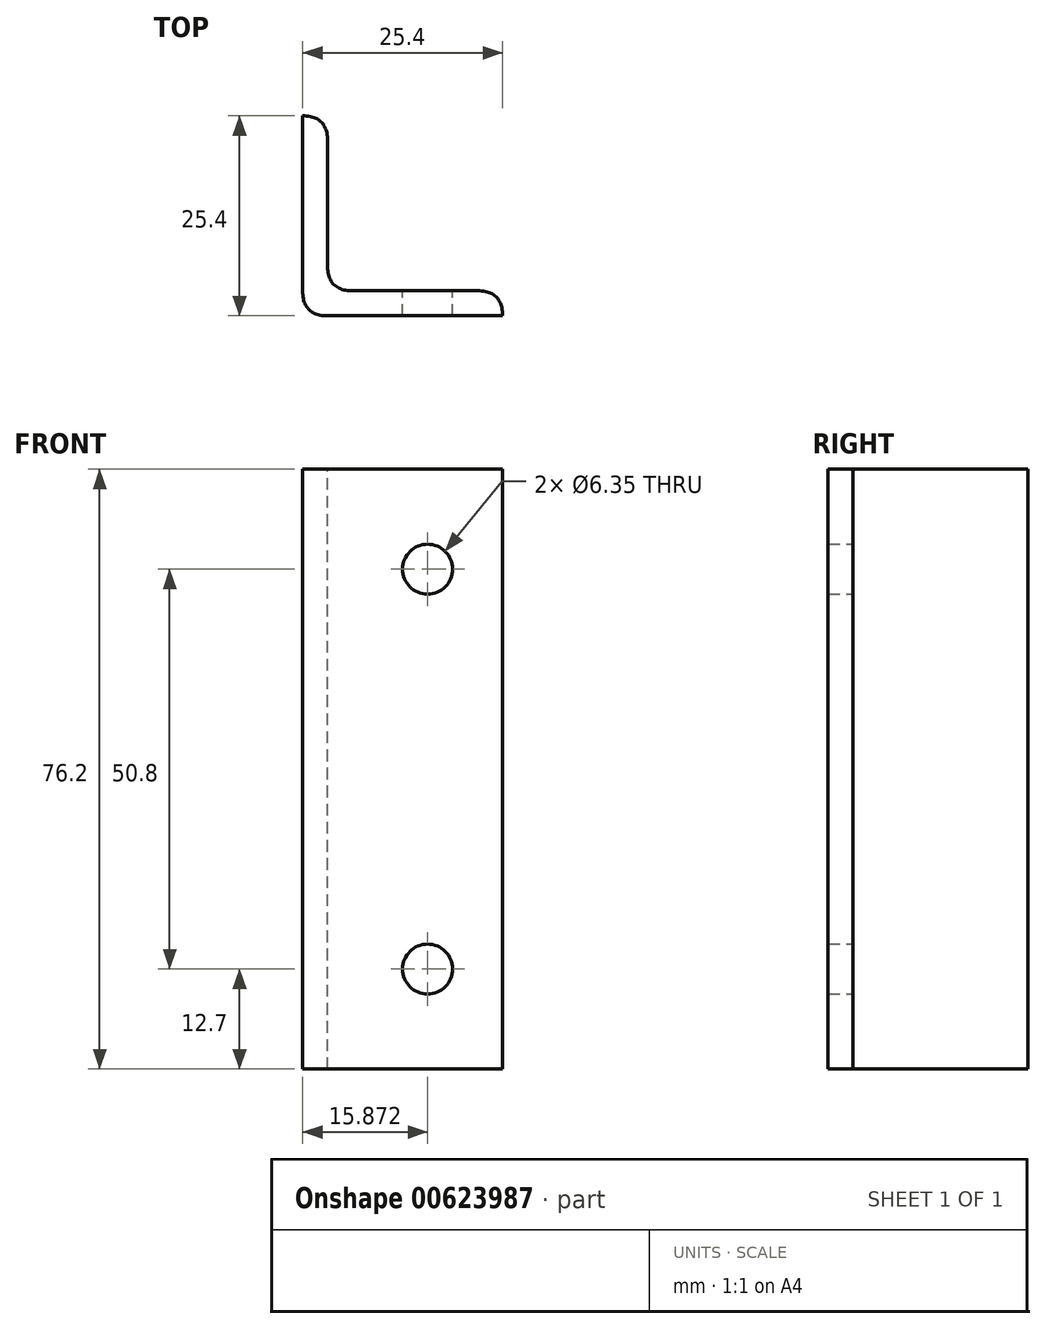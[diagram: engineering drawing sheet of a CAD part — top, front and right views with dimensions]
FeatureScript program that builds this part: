
annotation { "Feature Type Name" : "Feature", "Feature Type Description" : "" }
export const myFeature = defineFeature(function(context is Context, id is Id, definition is map)
    precondition{}
    {
        {
            var Q0;
            Q0=qCreatedBy(makeId("Top.planeOp"),FACE);
            var sketch = newSketch(context, id + "F0", { "sketchPlane" : qUnion([Q0])});
            skLineSegment(sketch, "E0", {"start": v(-37.22, 7.79) * mm, "end": v(-37.22, -17.61) * mm});
            skLineSegment(sketch, "E1", {"start": v(-37.22, -17.61) * mm, "end": v(-11.82, -17.61) * mm});
            skLineSegment(sketch, "E2", {"start": v(-11.82, -17.61) * mm, "end": v(-11.82, -14.44) * mm});
            skLineSegment(sketch, "E3", {"start": v(-11.82, -14.44) * mm, "end": v(-34.05, -14.44) * mm});
            skLineSegment(sketch, "E4", {"start": v(-34.05, -14.44) * mm, "end": v(-34.05, 7.79) * mm});
            skLineSegment(sketch, "E5", {"start": v(-34.05, 7.79) * mm, "end": v(-37.22, 7.79) * mm});
            skSolve(sketch);
        }
        {
            var Q0;
            Q0=makeQuery(id+"F0.imprint","IMPRINT",FACE,{"disambiguationData":[TD([[makeQuery(id+"F0.imprint","IMPRINT",EDGE,{"derivedFrom":sQuery(id+"F0.wireOp",EDGE,"E0")}),1.0]])]});
            extrude(context, id + "F1", {"entities" : qUnion([Q0]), "depth" : 76.2 * mm, "offsetDistance" : 25.4 * mm});
        }
        {
            var Q0;
            Q0=makeQuery(id+"F1.opExtrude","SWEPT_FACE",FACE,{"disambiguationData":[OSD([sQuery(id+"F0.wireOp",EDGE,"E3")])]});
            var sketch = newSketch(context, id + "F2", { "sketchPlane" : qUnion([Q0])});
            skCircle(sketch, "E6", {"center": v(21.35, 63.5) * mm, "radius": 3.18 * mm});
            skCircle(sketch, "E7", {"center": v(21.35, 12.7) * mm, "radius": 3.18 * mm});
            skSolve(sketch);
        }
        {
            var Q0;
            Q0=makeQuery(id+"F2.imprint","IMPRINT",FACE,{"disambiguationData":[TD([[makeQuery(id+"F2.imprint","IMPRINT",EDGE,{"derivedFrom":sQuery(id+"F2.wireOp",EDGE,"E6")}),1.0]])]});
            var Q1;
            Q1=makeQuery(id+"F2.imprint","IMPRINT",FACE,{"disambiguationData":[TD([[makeQuery(id+"F2.imprint","IMPRINT",EDGE,{"derivedFrom":sQuery(id+"F2.wireOp",EDGE,"E7")}),1.0]])]});
            extrude(context, id + "F3", {"entities" : qUnion([Q0, Q1]), "operationType" : NewBodyOperationType.REMOVE, "oppositeDirection" : true, "depth" : 3.17 * mm, "offsetDistance" : 25.4 * mm});
        }
        {
            var Q0;
            Q0=makeQuery(id+"F1.opExtrude","SWEPT_EDGE",EDGE,{"disambiguationData":[OSD([sQuery(id+"F0.wireOp",EDGE,"E3"),sQuery(id+"F0.wireOp",EDGE,"E4")])]});
            var Q1;
            Q1=makeQuery(id+"F1.opExtrude","SWEPT_EDGE",EDGE,{"disambiguationData":[OSD([sQuery(id+"F0.wireOp",EDGE,"E2"),sQuery(id+"F0.wireOp",EDGE,"E3")])]});
            var Q2;
            Q2=makeQuery(id+"F1.opExtrude","SWEPT_EDGE",EDGE,{"disambiguationData":[OSD([sQuery(id+"F0.wireOp",EDGE,"E4"),sQuery(id+"F0.wireOp",EDGE,"E5")])]});
            var Q3;
            Q3=makeQuery(id+"F1.opExtrude","SWEPT_EDGE",EDGE,{"disambiguationData":[OSD([sQuery(id+"F0.wireOp",EDGE,"E0"),sQuery(id+"F0.wireOp",EDGE,"E1")])]});
            fillet(context, id + "F4", {"entities" : qUnion([Q0, Q1, Q2, Q3]), "radius" : 3.17 * mm, "tangentPropagation" : true, "rho" : 0.5, "crossSection" : FilletCrossSection.CONIC, "allowEdgeOverflow" : false});
        }
    });
